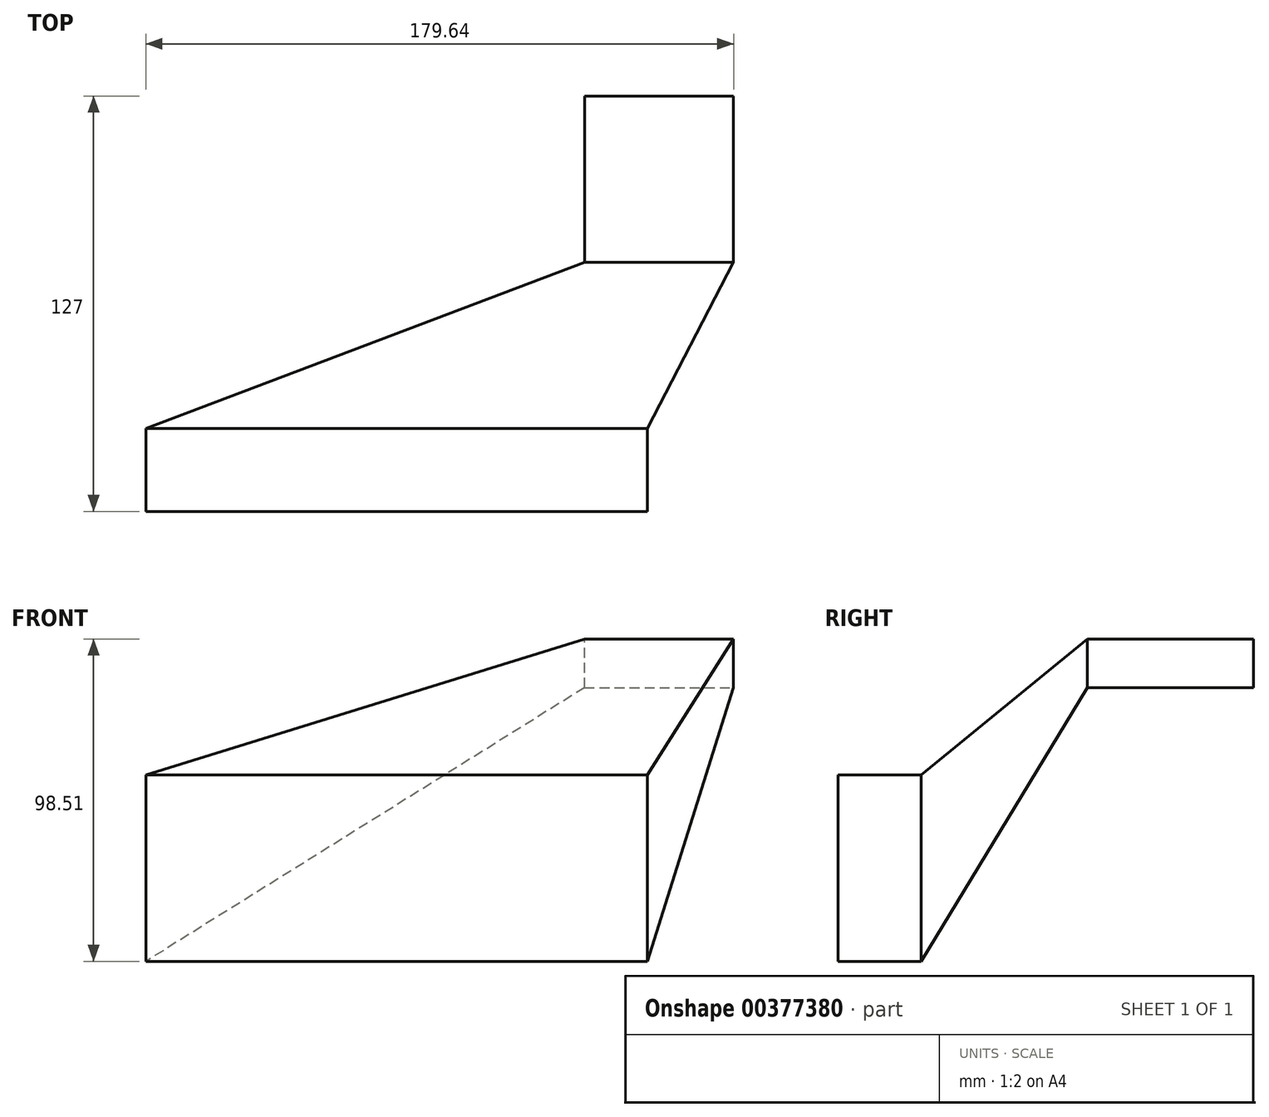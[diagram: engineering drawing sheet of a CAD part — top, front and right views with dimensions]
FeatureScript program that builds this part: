
annotation { "Feature Type Name" : "Feature", "Feature Type Description" : "" }
export const myFeature = defineFeature(function(context is Context, id is Id, definition is map)
    precondition{}
    {
        {
            var Q0;
            Q0=qCreatedBy(makeId("Front.planeOp"),FACE);
            var sketch = newSketch(context, id + "F0", { "sketchPlane" : qUnion([Q0])});
            skLineSegment(sketch, "E0.bottom", {"start": v(-134.07, 25.44) * mm, "end": v(19.17, 25.44) * mm});
            skLineSegment(sketch, "E0.top", {"start": v(-134.07, -31.49) * mm, "end": v(19.17, -31.49) * mm});
            skLineSegment(sketch, "E0.left", {"start": v(-134.07, 25.44) * mm, "end": v(-134.07, -31.49) * mm});
            skLineSegment(sketch, "E0.right", {"start": v(19.17, 25.44) * mm, "end": v(19.17, -31.49) * mm});
            skLineSegment(sketch, "E1.bottom", {"start": v(0, 52.16) * mm, "end": v(45.57, 52.16) * mm});
            skLineSegment(sketch, "E1.top", {"start": v(0, 67.02) * mm, "end": v(45.57, 67.02) * mm});
            skLineSegment(sketch, "E1.left", {"start": v(0, 52.16) * mm, "end": v(0, 67.02) * mm});
            skLineSegment(sketch, "E1.right", {"start": v(45.57, 52.16) * mm, "end": v(45.57, 67.02) * mm});
            skSolve(sketch);
        }
        {
            var Q0;
            Q0=makeQuery(id+"F0.imprint","IMPRINT",FACE,{"disambiguationData":[TD([[makeQuery(id+"F0.imprint","IMPRINT",EDGE,{"derivedFrom":sQuery(id+"F0.wireOp",EDGE,"E0.bottom")}),-1.0]])]});
            extrude(context, id + "F1", {"entities" : qUnion([Q0]), "depth" : 25.4 * mm});
        }
        {
            var Q0;
            Q0=makeQuery(id+"F0.imprint","IMPRINT",FACE,{"disambiguationData":[TD([[makeQuery(id+"F0.imprint","IMPRINT",EDGE,{"derivedFrom":sQuery(id+"F0.wireOp",EDGE,"E1.bottom")}),1.0]])]});
            extrude(context, id + "F2", {"entities" : qUnion([Q0]), "depth" : -50.8 * mm});
        }
        {
            var Q0;
            Q0=makeQuery(id+"F2.opExtrude","SWEPT_BODY",BODY,{"disambiguationData":[OSD([sQuery(id+"F0.wireOp",EDGE,"E1.bottom"),sQuery(id+"F0.wireOp",EDGE,"E1.top"),sQuery(id+"F0.wireOp",EDGE,"E1.left"),sQuery(id+"F0.wireOp",EDGE,"E1.right")])]});
            transform(context, id + "F3", {"entities" : qUnion([Q0]), "transformType" : TransformType.TRANSLATION_3D, "dx" : 0 * mm, "dy" : 50.8 * mm, "dz" : 0 * mm, "makeCopy" : false});
        }
        {
            var Q0;
            Q0=makeQuery(id+"F2.opExtrude","CAP_FACE",FACE,{"disambiguationData":[OSD([sQuery(id+"F0.wireOp",EDGE,"E1.bottom"),sQuery(id+"F0.wireOp",EDGE,"E1.top"),sQuery(id+"F0.wireOp",EDGE,"E1.left"),sQuery(id+"F0.wireOp",EDGE,"E1.right")])],"isStart":true});
            var Q1;
            Q1=makeQuery(id+"F1.opExtrude","CAP_FACE",FACE,{"disambiguationData":[OSD([sQuery(id+"F0.wireOp",EDGE,"E0.bottom"),sQuery(id+"F0.wireOp",EDGE,"E0.top"),sQuery(id+"F0.wireOp",EDGE,"E0.left"),sQuery(id+"F0.wireOp",EDGE,"E0.right")])],"isStart":true});
            loft(context, id + "F4", {"sheetProfilesArray" : [{ "sheetProfileEntities" : qUnion([Q0]) }, { "sheetProfileEntities" : qUnion([Q1]) }]});
        }
    });
